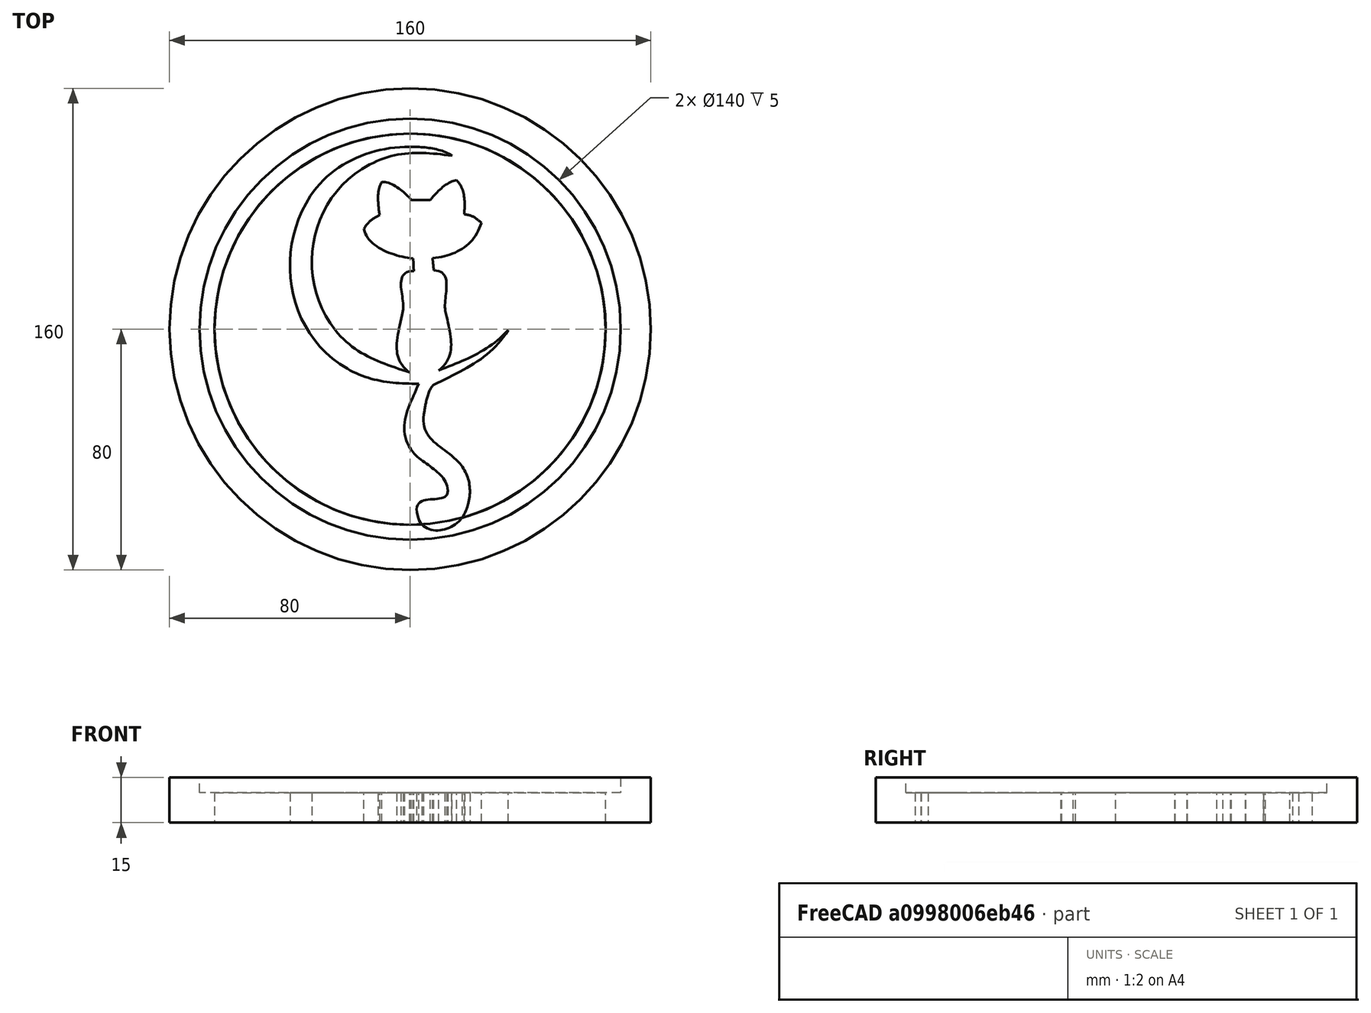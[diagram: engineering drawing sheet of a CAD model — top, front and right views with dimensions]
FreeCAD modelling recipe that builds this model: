
FCSTD DOCUMENT  (FreeCAD 0.19RUnknown)
Label: Cat_lamp
License: All rights reserved
LicenseURL: http://en.wikipedia.org/wiki/All_rights_reserved
objects: Sketcher::SketchObject×5, PartDesign::Pad×3, PartDesign::Body×3, TechDraw::DrawViewDimension×3, PartDesign::Pocket×2, Part::FeaturePython×2, App::Part×2, Spreadsheet::Sheet×1, Part::Feature×1, PartDesign::Boolean×1, PartDesign::FeatureBase×1, TechDraw::DrawSVGTemplate×1, TechDraw::DrawViewPart×1, TechDraw::DrawPage×1
note: 23 computed .brp shape members not serialized (recipe doc carries the construction recipe); baked Part::Feature solids carry a one-line shape summary decoded from their .brp

FEATURE [Sketcher::SketchObject] Sketch
  FullyConstrained = true
  MapMode = 5
  Support = -> [XY_Plane001]
  expr: Constraints[1] = <<pmters>>.r_outer
  expr: Constraints[2] = <<pmters>>.r_inner
  sketch-geometry (2):
    g0: Circle CenterX=0 CenterY=0 CenterZ=0 NormalX=0 NormalY=0 NormalZ=1 AngleXU=0 Radius=80
    g1: Circle CenterX=0 CenterY=0 CenterZ=0 NormalX=0 NormalY=0 NormalZ=1 AngleXU=0 Radius=65
  constraints (4):
    c: Coincident(g0,g-1)
    c: Radius(g0) = 80
    c: Radius(g1) = 65
    c: Coincident(g1,g0)
FEATURE [Spreadsheet::Sheet] Spreadsheet  label="pmters"
  cells = A1=r_outer; B1(r_outer)=80; A2=r_delta; B2(r_delta)=15; C2=debljina lampe /2; A3=r_inner; B3(r_inner)==r_outer - r_delta; A5=r_led_delta; B5(r_led_delta)=5; C5=udubljenje led ; A6=r_led_outer; B6(r_led_outer)==r_inner + r_led_delta; A7=r_led_inner; B7(r_led_inner)==r_inner; A8=h_led; B8(h_led)=5; C8=sirina led trake /2; A9=debljina dizajna; B9(design_width)==r_delta - h_led
FEATURE [PartDesign::Pad] Pad
  Direction = (1,1,1)
  Length = 15
  Length2 = 100
  Profile = -> Sketch
  Type = 0
  expr: Length = <<pmters>>.r_delta
FEATURE [Sketcher::SketchObject] Sketch001
  FullyConstrained = true
  MapMode = 5
  Placement = pos=(0,0,15) rot=(0,0,1;0rad)
  Support = -> [Pad]
  expr: Constraints[2] = <<pmters>>.r_led_inner
  expr: Constraints[3] = <<pmters>>.r_led_outer
  sketch-geometry (2):
    g0: Circle CenterX=0 CenterY=0 CenterZ=0 NormalX=0 NormalY=0 NormalZ=1 AngleXU=0 Radius=70
    g1: Circle CenterX=0 CenterY=0 CenterZ=0 NormalX=0 NormalY=0 NormalZ=1 AngleXU=0 Radius=65
  constraints (4):
    c: Coincident(g0,g-1)
    c: Coincident(g1,g0)
    c: Radius(g1) = 65
    c: Radius(g0) = 70
FEATURE [PartDesign::Pocket] Pocket  label="led_pocket"
  BaseFeature = -> Pad
  Length = 5
  Length2 = 100
  Profile = -> Sketch001
  Type = 0
  expr: Length = <<pmters>>.h_led
FEATURE [Part::Feature] path1820  label="design"
  Placement = pos=(-7,17,0) rot=(0,0,1;0rad)
  shape: bbox 27.76 x 46.14 x 2e-07 mm, 1 faces, 0 solids (baked)
FEATURE [Part::FeaturePython] Clone  label="design002"  # WARN: FeaturePython — macro-defined, semantics opaque (R4)
  AttacherType = Attacher::AttachEngine3D
  Fuse = false
  Placement = pos=(-29.4346,33.9344,0) rot=(0,0,1;0rad)
  Scale = (1.87167,1.87167,1.87167)
FEATURE [Part::FeaturePython] Clone001  label="design003"  # Draft clone (typed FeaturePython)
  AttacherType = Attacher::AttachEngine3D
  Fuse = false
  Objects = -> [Clone]
  Placement = pos=(-39.9613,60.6264,0) rot=(0,0,1;0rad)
  Scale = (1.5,1.5,1.5)
FEATURE [Sketcher::SketchObject] Sketch004
  FullyConstrained = false
  sketch-geometry (33):
    g0: BSplineCurve PolesCount=4 KnotsCount=2 Degree=3 IsPeriodic=0
    g1: BSplineCurve PolesCount=4 KnotsCount=2 Degree=3 IsPeriodic=0
    g2: BSplineCurve PolesCount=4 KnotsCount=2 Degree=3 IsPeriodic=0
    g3: BSplineCurve PolesCount=4 KnotsCount=2 Degree=3 IsPeriodic=0
    g4: BSplineCurve PolesCount=4 KnotsCount=2 Degree=3 IsPeriodic=0
    g5: BSplineCurve PolesCount=4 KnotsCount=2 Degree=3 IsPeriodic=0
    g6: BSplineCurve PolesCount=4 KnotsCount=2 Degree=3 IsPeriodic=0
    g7: BSplineCurve PolesCount=4 KnotsCount=2 Degree=3 IsPeriodic=0
    g8: BSplineCurve PolesCount=4 KnotsCount=2 Degree=3 IsPeriodic=0
    g9: BSplineCurve PolesCount=4 KnotsCount=2 Degree=3 IsPeriodic=0
    g10: BSplineCurve PolesCount=4 KnotsCount=2 Degree=3 IsPeriodic=0
    g11: BSplineCurve PolesCount=4 KnotsCount=2 Degree=3 IsPeriodic=0
    g12: BSplineCurve PolesCount=2 KnotsCount=2 Degree=1 IsPeriodic=0
    g13: BSplineCurve PolesCount=4 KnotsCount=2 Degree=3 IsPeriodic=0
    g14: BSplineCurve PolesCount=4 KnotsCount=2 Degree=3 IsPeriodic=0
    g15: BSplineCurve PolesCount=4 KnotsCount=2 Degree=3 IsPeriodic=0
    g16: BSplineCurve PolesCount=4 KnotsCount=2 Degree=3 IsPeriodic=0
    g17: BSplineCurve PolesCount=2 KnotsCount=2 Degree=1 IsPeriodic=0
    g18: BSplineCurve PolesCount=4 KnotsCount=2 Degree=3 IsPeriodic=0
    g19: BSplineCurve PolesCount=4 KnotsCount=2 Degree=3 IsPeriodic=0
    g20: BSplineCurve PolesCount=4 KnotsCount=2 Degree=3 IsPeriodic=0
    g21: BSplineCurve PolesCount=4 KnotsCount=2 Degree=3 IsPeriodic=0
    g22: BSplineCurve PolesCount=2 KnotsCount=2 Degree=1 IsPeriodic=0
    g23: BSplineCurve PolesCount=4 KnotsCount=2 Degree=3 IsPeriodic=0
    g24: BSplineCurve PolesCount=4 KnotsCount=2 Degree=3 IsPeriodic=0
    g25: BSplineCurve PolesCount=4 KnotsCount=2 Degree=3 IsPeriodic=0
    g26: BSplineCurve PolesCount=4 KnotsCount=2 Degree=3 IsPeriodic=0
    g27: BSplineCurve PolesCount=4 KnotsCount=2 Degree=3 IsPeriodic=0
    g28: BSplineCurve PolesCount=4 KnotsCount=2 Degree=3 IsPeriodic=0
    g29: BSplineCurve PolesCount=4 KnotsCount=2 Degree=3 IsPeriodic=0
    g30: BSplineCurve PolesCount=4 KnotsCount=2 Degree=3 IsPeriodic=0
    g31: BSplineCurve PolesCount=4 KnotsCount=2 Degree=3 IsPeriodic=0
    g32: BSplineCurve PolesCount=2 KnotsCount=2 Degree=1 IsPeriodic=0
  constraints (33):
    c: Coincident(g0,g1)
    c: Coincident(g1,g2)
    c: Coincident(g2,g3)
    c: Coincident(g3,g4)
    c: Coincident(g4,g5)
    c: Coincident(g5,g6)
    c: Coincident(g6,g7)
    c: Coincident(g7,g8)
    c: Coincident(g8,g9)
    c: Coincident(g9,g10)
    c: Coincident(g10,g11)
    c: Coincident(g11,g12)
    c: Coincident(g12,g13)
    c: Coincident(g13,g14)
    c: Coincident(g14,g15)
    c: Coincident(g15,g16)
    c: Coincident(g16,g17)
    c: Coincident(g17,g18)
    c: Coincident(g18,g19)
    c: Coincident(g19,g20)
    c: Coincident(g20,g21)
    c: Coincident(g21,g22)
    c: Coincident(g22,g23)
    c: Coincident(g23,g24)
    c: Coincident(g24,g25)
    c: Coincident(g25,g26)
    c: Coincident(g26,g27)
    c: Coincident(g27,g28)
    c: Coincident(g28,g29)
    c: Coincident(g29,g30)
    c: Coincident(g30,g31)
    c: Coincident(g31,g32)
    c: Coincident(g32,g0)
FEATURE [PartDesign::Pad] Pad002
  Direction = (1,1,1)
  Length = 10
  Length2 = 100
  Profile = -> Sketch004
  Type = 0
  expr: Length = <<pmters>>.design_width
FEATURE [PartDesign::Body] Body002  label="design005"
  Group = -> [Sketch004,Pad002]
  Origin = -> Origin004
  Tip = -> Pad002
FEATURE [PartDesign::Boolean] Boolean
  BaseFeature = -> Pocket
  Group = -> [Body002]
  Type = 0
FEATURE [PartDesign::Body] Body  label="half_lamp_with design"
  Group = -> [Sketch,Pad,Sketch001,Pocket,Boolean]
  Origin = -> Origin001
  Tip = -> Boolean
FEATURE [App::Part] Part001  label="lamp_design3"
  Group = -> [Body]
  Origin = -> Origin002
FEATURE [Sketcher::SketchObject] Sketch005
  FullyConstrained = true
  MapMode = 5
  expr: Constraints[2] = <<pmters>>.r_inner
  expr: Constraints[1] = <<pmters>>.r_outer
  sketch-geometry (2):
    g0: Circle CenterX=0 CenterY=0 CenterZ=0 NormalX=0 NormalY=0 NormalZ=1 AngleXU=0 Radius=80
    g1: Circle CenterX=0 CenterY=0 CenterZ=0 NormalX=0 NormalY=0 NormalZ=1 AngleXU=0 Radius=65
  constraints (4):
    c: Coincident(g0,g-1)
    c: Radius(g0) = 80
    c: Radius(g1) = 65
    c: Coincident(g1,g0)
FEATURE [PartDesign::Pad] Pad003
  Direction = (1,1,1)
  Length = 15
  Length2 = 100
  Profile = -> Sketch005
  Type = 0
  expr: Length = <<pmters>>.r_delta
FEATURE [Sketcher::SketchObject] Sketch006
  FullyConstrained = true
  MapMode = 5
  Placement = pos=(0,0,15) rot=(0,0,1;0rad)
  Support = -> [Pad003]
  expr: Constraints[3] = <<pmters>>.r_led_outer
  expr: Constraints[2] = <<pmters>>.r_led_inner
  sketch-geometry (2):
    g0: Circle CenterX=0 CenterY=0 CenterZ=0 NormalX=0 NormalY=0 NormalZ=1 AngleXU=0 Radius=70
    g1: Circle CenterX=0 CenterY=0 CenterZ=0 NormalX=0 NormalY=0 NormalZ=1 AngleXU=0 Radius=65
  constraints (4):
    c: Coincident(g0,g-1)
    c: Coincident(g1,g0)
    c: Radius(g1) = 65
    c: Radius(g0) = 70
FEATURE [PartDesign::Pocket] Pocket001  label="led_pocket001"
  BaseFeature = -> Pad003
  Length = 5
  Length2 = 100
  Profile = -> Sketch006
  Type = 0
  expr: Length = <<pmters>>.h_led
FEATURE [PartDesign::FeatureBase] BaseFeature
  BaseFeature = -> Pocket001
FEATURE [PartDesign::Body] Body003
  BaseFeature = -> Pocket001
  Group = -> [BaseFeature]
  Origin = -> Origin005
  Tip = -> BaseFeature
FEATURE [App::Part] Part  label="half_lamp"
  Group = -> [Body003]
  Origin = -> Origin
FEATURE [TechDraw::DrawSVGTemplate] Template
  EditableTexts = Designed_by_Name=Designed by Name; Drawing_number=Drawing number; FC-Date=Date; FC-SC=Scale; FC-SH=Sheet; FC-Title=Title; Subtitle=Subtitle; Weight=Weight
  Height = 210
  Orientation = 1
  Width = 297
FEATURE [TechDraw::DrawViewPart] View
  CoarseView = false
  Direction = (0,0,1)
  Focus = 100
  HardHidden = false
  IsoCount = 0
  IsoHidden = false
  IsoVisible = false
  LockPosition = false
  Perspective = false
  Rotation = 0
  ScaleType = 0
  SeamHidden = false
  SeamVisible = true
  SmoothHidden = false
  SmoothVisible = true
  Source = -> [Part001]
  X = 92.7796
  XDirection = (1,0,0)
  Y = 117.282
FEATURE [TechDraw::DrawViewDimension] Dimension
  Arbitrary = false
  ArbitraryTolerances = false
  EqualTolerance = true
  FormatSpec = %.2f
  FormatSpecOverTolerance = %+.2f
  FormatSpecUnderTolerance = %+.2f
  Inverted = false
  LockPosition = false
  MeasureType = 1
  OverTolerance = 0
  References2D = -> [View]
  Rotation = 0
  ScaleType = 0
  TheoreticalExact = false
  Type = 0
  UnderTolerance = 0
  X = 68.0991
  Y = 79.6862
FEATURE [TechDraw::DrawViewDimension] Dimension001
  Arbitrary = false
  ArbitraryTolerances = false
  EqualTolerance = true
  FormatSpec = R%.2f
  FormatSpecOverTolerance = %+.2f
  FormatSpecUnderTolerance = %+.2f
  Inverted = false
  LockPosition = false
  MeasureType = 1
  OverTolerance = 0
  References2D = -> [View]
  Rotation = 0
  ScaleType = 0
  TheoreticalExact = false
  Type = 4
  UnderTolerance = 0
  X = 134.208
  Y = 7.78887
FEATURE [TechDraw::DrawViewDimension] Dimension002
  Arbitrary = false
  ArbitraryTolerances = false
  EqualTolerance = true
  FormatSpec = R%.2f
  FormatSpecOverTolerance = %+.2f
  FormatSpecUnderTolerance = %+.2f
  Inverted = false
  LockPosition = false
  MeasureType = 1
  OverTolerance = 0
  References2D = -> [View]
  Rotation = 0
  ScaleType = 0
  TheoreticalExact = false
  Type = 4
  UnderTolerance = 0
  X = 125.82
  Y = 20.0713
FEATURE [TechDraw::DrawPage] Page
  KeepUpdated = true
  NextBalloonIndex = 1
  ProjectionType = 0
  Template = -> Template
  Views = -> [View,Dimension,Dimension001,Dimension002]
